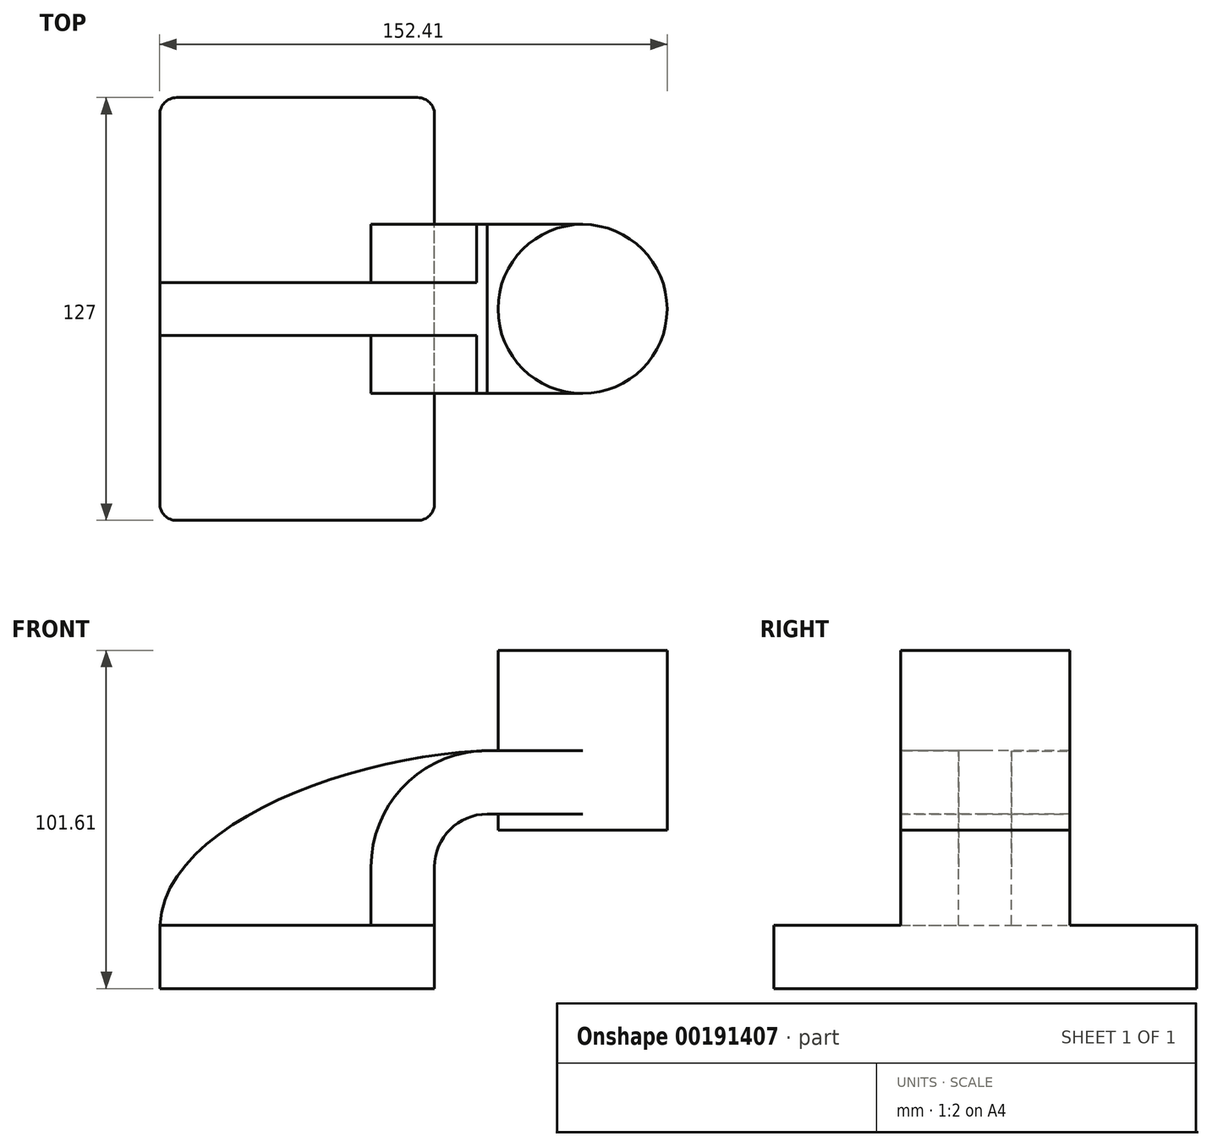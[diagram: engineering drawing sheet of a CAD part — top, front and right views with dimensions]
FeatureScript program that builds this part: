
annotation { "Feature Type Name" : "Feature", "Feature Type Description" : "" }
export const myFeature = defineFeature(function(context is Context, id is Id, definition is map)
    precondition{}
    {
        {
            var Q0;
            Q0=qCreatedBy(makeId("Front.planeOp"),FACE);
            var sketch = newSketch(context, id + "F0", { "sketchPlane" : qUnion([Q0])});
            skLineSegment(sketch, "E0.rect.bottom", {"start": v(-41.28, 9.52) * mm, "end": v(41.28, 9.52) * mm});
            skLineSegment(sketch, "E0.rect.top", {"start": v(-41.28, -9.52) * mm, "end": v(41.28, -9.52) * mm});
            skLineSegment(sketch, "E0.rect.left", {"start": v(-41.28, 9.52) * mm, "end": v(-41.28, -9.52) * mm});
            skLineSegment(sketch, "E0.rect.right", {"start": v(41.28, 9.52) * mm, "end": v(41.28, -9.52) * mm});
            skPoint(sketch, "E0.rect.middle", {"position": v(0, 0) * mm});
            skLineSegment(sketch, "E1", {"start": v(41.28, 9.52) * mm, "end": v(41.28, 27) * mm});
            skArc(sketch, "E2", {"start": v(41.28, 27) * mm, "mid": v(45.92, 38.23) * mm, "end": v(57.15, 42.88) * mm});
            skLineSegment(sketch, "E3", {"start": v(57.15, 42.88) * mm, "end": v(85.72, 42.88) * mm});
            skLineSegment(sketch, "E4.rect.bottom", {"start": v(60.32, 38.1) * mm, "end": v(111.12, 38.1) * mm});
            skLineSegment(sketch, "E4.rect.top", {"start": v(60.32, 66.68) * mm, "end": v(111.12, 66.68) * mm});
            skLineSegment(sketch, "E4.rect.left", {"start": v(60.32, 38.1) * mm, "end": v(60.32, 66.68) * mm});
            skLineSegment(sketch, "E4.rect.right", {"start": v(111.13, 38.1) * mm, "end": v(111.12, 66.68) * mm});
            skPoint(sketch, "E4.rect.middle", {"position": v(85.72, 52.39) * mm});
            skLineSegment(sketch, "E5.0", {"start": v(57.15, 61.93) * mm, "end": v(85.72, 61.93) * mm});
            skArc(sketch, "E5.1", {"start": v(22.23, 27) * mm, "mid": v(32.45, 51.7) * mm, "end": v(57.15, 61.93) * mm});
            skLineSegment(sketch, "E5.2", {"start": v(22.23, 9.52) * mm, "end": v(22.23, 27) * mm});
            skLineSegment(sketch, "E6", {"start": v(85.72, 38.1) * mm, "end": v(85.72, 66.68) * mm});
            skFitSpline(sketch, "E7", {"points": [v(-41.28, 9.53) * mm, v(57.15, 61.93) * mm], "startDerivative": vector(5.2, 92.34) * mm, "endDerivative": vector(120.92, 4.22) * mm});
            skSolve(sketch);
        }
        {
            var Q0;
            Q0=makeQuery(id+"F0.imprint","IMPRINT",FACE,{"disambiguationData":[TD([[makeQuery(id+"F0.imprint","IMPRINT",EDGE,{"derivedFrom":sQuery(id+"F0.wireOp",EDGE,"E0.rect.top")}),1.0]])]});
            extrude(context, id + "F1", {"entities" : qUnion([Q0]), "endBound" : BoundingType.SYMMETRIC, "depth" : 127 * mm});
        }
        {
            var Q0;
            {var subQ9=sQuery(id+"F0.wireOp",EDGE,"E1");Q0=makeQuery(id+"F0.imprint","IMPRINT",FACE,{"disambiguationData":[TD([[makeQuery(id+"F0.imprint","IMPRINT",EDGE,{"derivedFrom":subQ9}),1.0]])]});}
            var Q1;
            {var subQ0=sQuery(id+"F0.wireOp",EDGE,"E6");var subQ1=sQuery(id+"F0.wireOp",EDGE,"E3");var subQ2=makeQuery(id+"F0.imprint","INTERSECT",VERTEX,{"derivedFrom":[subQ1,subQ0]});Q1=makeQuery(id+"F0.imprint","IMPRINT",FACE,{"disambiguationData":[TD([[makeQuery(id+"F0.imprint","IMPRINT",EDGE,{"disambiguationData":[TD([[subQ2,1.0]])],"derivedFrom":subQ1}),1.0]])]});}
            extrude(context, id + "F2", {"entities" : qUnion([Q0, Q1]), "operationType" : NewBodyOperationType.ADD, "endBound" : BoundingType.SYMMETRIC, "depth" : 50.8 * mm});
        }
        {
            var Q0;
            {var subQ3=sQuery(id+"F0.wireOp",EDGE,"E5.2");Q0=makeQuery(id+"F0.imprint","IMPRINT",FACE,{"disambiguationData":[TD([[makeQuery(id+"F0.imprint","IMPRINT",EDGE,{"derivedFrom":subQ3}),1.0]])]});}
            extrude(context, id + "F3", {"entities" : qUnion([Q0]), "operationType" : NewBodyOperationType.ADD, "endBound" : BoundingType.SYMMETRIC, "depth" : 15.88 * mm});
        }
        {
            var Q0;
            {var subQ5=sQuery(id+"F0.wireOp",EDGE,"E4.rect.right");Q0=makeQuery(id+"F0.imprint","IMPRINT",FACE,{"disambiguationData":[TD([[makeQuery(id+"F0.imprint","IMPRINT",EDGE,{"derivedFrom":subQ5}),1.0]])]});}
            var Q1;
            Q1=sQuery(id+"F0.wireOp",EDGE,"E6");
            revolve(context, id + "F4", {"operationType" : NewBodyOperationType.ADD, "entities" : qUnion([Q0]), "axis" : qUnion([Q1]), "revolveType" : RevolveType.FULL});
        }
        {
            var Q0;
            Q0=makeQuery(id+"F1.opExtrude","CAP_EDGE",EDGE,{"disambiguationData":[OSD([sQuery(id+"F0.wireOp",EDGE,"E0.rect.right")])],"isStart":false});
            var Q1;
            Q1=makeQuery(id+"F1.opExtrude","CAP_EDGE",EDGE,{"disambiguationData":[OSD([sQuery(id+"F0.wireOp",EDGE,"E0.rect.left")])],"isStart":false});
            var Q2;
            Q2=makeQuery(id+"F1.opExtrude","CAP_EDGE",EDGE,{"disambiguationData":[OSD([sQuery(id+"F0.wireOp",EDGE,"E0.rect.right")])],"isStart":true});
            var Q3;
            Q3=makeQuery(id+"F1.opExtrude","CAP_EDGE",EDGE,{"disambiguationData":[OSD([sQuery(id+"F0.wireOp",EDGE,"E0.rect.left")])],"isStart":true});
            fillet(context, id + "F5", {"entities" : qUnion([Q0, Q1, Q2, Q3]), "radius" : 5.08 * mm, "tangentPropagation" : true, "allowEdgeOverflow" : false});
        }
        {
            var Q0;
            Q0=makeQuery(id+"F4.opRevolve","SWEPT_FACE",FACE,{"disambiguationData":[OSD([sQuery(id+"F0.wireOp",EDGE,"E4.rect.top")])]});
            extrude(context, id + "F6", {"entities" : qUnion([Q0]), "operationType" : NewBodyOperationType.ADD, "depth" : 25.4 * mm});
        }
    });
